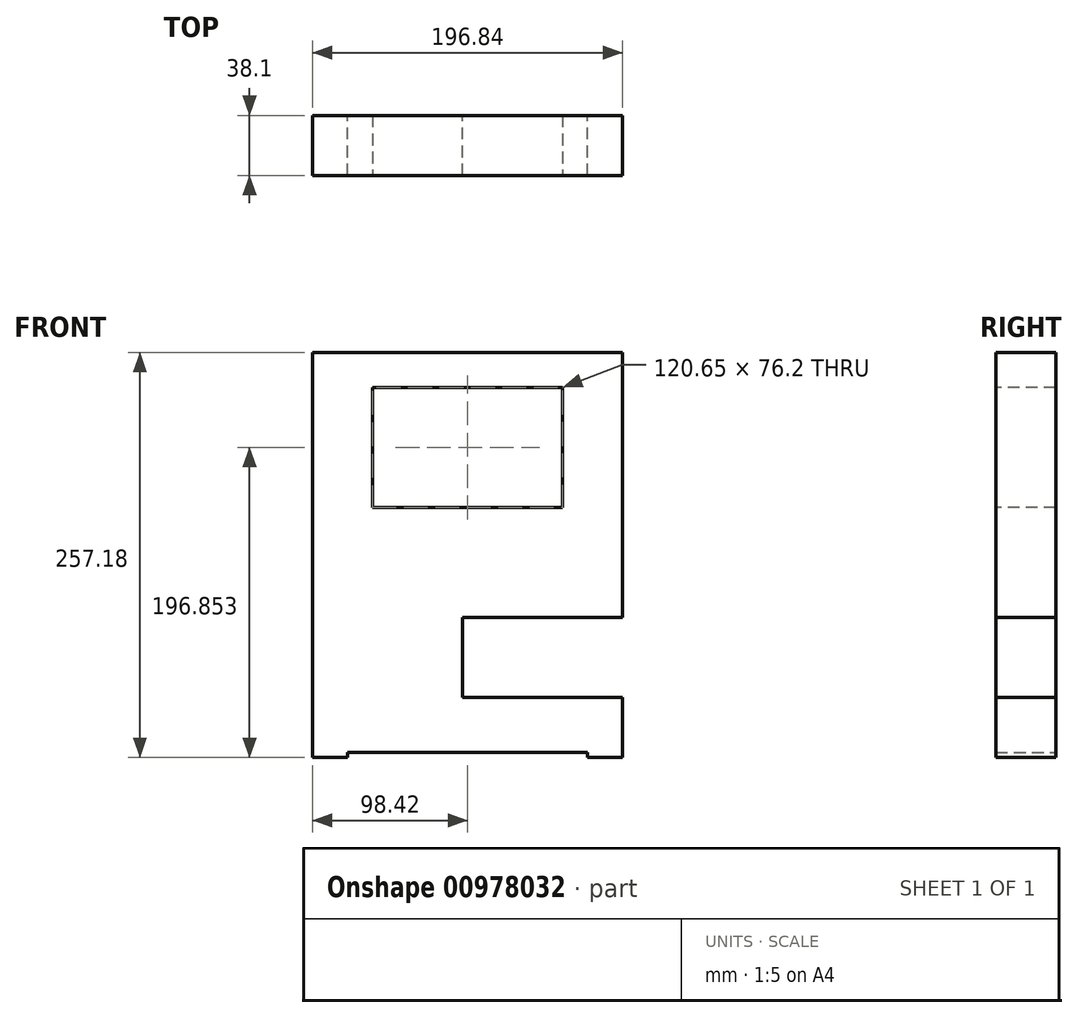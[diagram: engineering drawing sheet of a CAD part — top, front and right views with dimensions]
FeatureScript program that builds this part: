
annotation { "Feature Type Name" : "Feature", "Feature Type Description" : "" }
export const myFeature = defineFeature(function(context is Context, id is Id, definition is map)
    precondition{}
    {
        {
            var Q0;
            Q0=qCreatedBy(makeId("Front.planeOp"),FACE);
            var sketch = newSketch(context, id + "F0", { "sketchPlane" : qUnion([Q0])});
            skLineSegment(sketch, "E0", {"start": v(0, 128.59) * mm, "end": v(0, -128.59) * mm, "construction": true});
            skLineSegment(sketch, "E1", {"start": v(-98.42, 0) * mm, "end": v(98.43, 0) * mm, "construction": true});
            skLineSegment(sketch, "E2.bottom", {"start": v(-98.42, 128.59) * mm, "end": v(98.43, 128.59) * mm});
            skLineSegment(sketch, "E2.top", {"start": v(-98.42, -128.59) * mm, "end": v(98.43, -128.59) * mm});
            skLineSegment(sketch, "E2.left", {"start": v(-98.42, 128.59) * mm, "end": v(-98.42, -128.59) * mm});
            skLineSegment(sketch, "E2.right", {"start": v(98.43, 128.59) * mm, "end": v(98.43, -128.59) * mm});
            skLineSegment(sketch, "E3.bottom", {"start": v(-76.2, -128.59) * mm, "end": v(76.2, -128.59) * mm});
            skLineSegment(sketch, "E3.top", {"start": v(-76.2, -125.41) * mm, "end": v(76.2, -125.41) * mm});
            skLineSegment(sketch, "E3.left", {"start": v(-76.2, -128.59) * mm, "end": v(-76.2, -125.41) * mm});
            skLineSegment(sketch, "E3.right", {"start": v(76.2, -128.59) * mm, "end": v(76.2, -125.41) * mm});
            skLineSegment(sketch, "E4.bottom", {"start": v(98.43, -39.69) * mm, "end": v(-3.17, -39.69) * mm});
            skLineSegment(sketch, "E4.top", {"start": v(98.43, -90.49) * mm, "end": v(-3.17, -90.49) * mm});
            skLineSegment(sketch, "E4.left", {"start": v(98.43, -39.69) * mm, "end": v(98.43, -90.49) * mm});
            skLineSegment(sketch, "E4.right", {"start": v(-3.17, -39.69) * mm, "end": v(-3.17, -90.49) * mm});
            skSolve(sketch);
        }
        {
            var Q0;
            {var subQ8=sQuery(id+"F0.wireOp",EDGE,"E2.bottom");Q0=makeQuery(id+"F0.imprint","IMPRINT",FACE,{"disambiguationData":[TD([[makeQuery(id+"F0.imprint","IMPRINT",EDGE,{"derivedFrom":subQ8}),-1.0]])]});}
            extrude(context, id + "F1", {"entities" : qUnion([Q0]), "depth" : 38.1 * mm, "offsetDistance" : 25.4 * mm});
        }
        {
            var Q0;
            Q0=makeQuery(id+"F1.opExtrude","CAP_FACE",FACE,{"disambiguationData":[OSD([sQuery(id+"F0.wireOp",EDGE,"E2.bottom"),sQuery(id+"F0.wireOp",EDGE,"E2.top"),sQuery(id+"F0.wireOp",EDGE,"E2.left"),sQuery(id+"F0.wireOp",EDGE,"E2.right"),sQuery(id+"F0.wireOp",EDGE,"E3.top"),sQuery(id+"F0.wireOp",EDGE,"E3.left"),sQuery(id+"F0.wireOp",EDGE,"E3.right"),sQuery(id+"F0.wireOp",EDGE,"E4.bottom"),sQuery(id+"F0.wireOp",EDGE,"E4.top"),sQuery(id+"F0.wireOp",EDGE,"E4.right")])],"isStart":false});
            var sketch = newSketch(context, id + "F2", { "sketchPlane" : qUnion([Q0])});
            skLineSegment(sketch, "E5.bottom", {"start": v(-60.32, 106.36) * mm, "end": v(60.33, 106.36) * mm});
            skLineSegment(sketch, "E5.top", {"start": v(-60.32, 30.16) * mm, "end": v(60.33, 30.16) * mm});
            skLineSegment(sketch, "E5.left", {"start": v(-60.32, 106.36) * mm, "end": v(-60.32, 30.16) * mm});
            skLineSegment(sketch, "E5.right", {"start": v(60.33, 106.36) * mm, "end": v(60.33, 30.16) * mm});
            skLineSegment(sketch, "E6", {"start": v(0, 128.59) * mm, "end": v(0, -125.41) * mm, "construction": true});
            skSolve(sketch);
        }
        {
            var Q0;
            Q0=makeQuery(id+"F2.imprint","IMPRINT",FACE,{"disambiguationData":[TD([[makeQuery(id+"F2.imprint","IMPRINT",EDGE,{"derivedFrom":sQuery(id+"F2.wireOp",EDGE,"E5.bottom")}),-1.0]])]});
            extrude(context, id + "F3", {"entities" : qUnion([Q0]), "operationType" : NewBodyOperationType.REMOVE, "endBound" : BoundingType.THROUGH_ALL, "oppositeDirection" : true, "depth" : 25.4 * mm, "offsetDistance" : 25.4 * mm});
        }
    });
